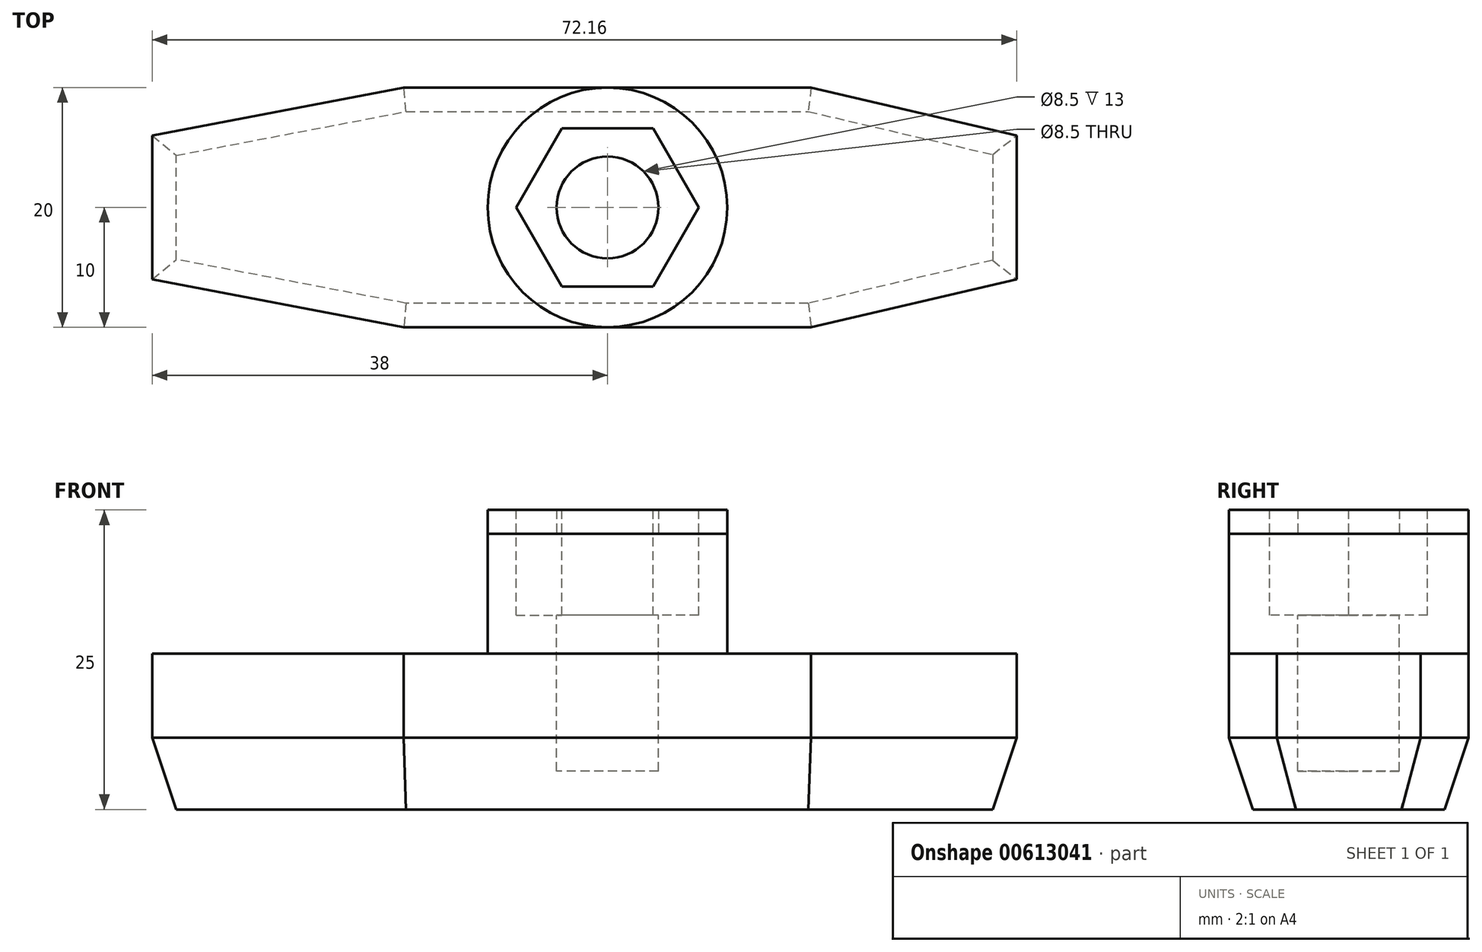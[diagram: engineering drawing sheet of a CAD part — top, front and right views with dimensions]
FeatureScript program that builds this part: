
annotation { "Feature Type Name" : "Feature", "Feature Type Description" : "" }
export const myFeature = defineFeature(function(context is Context, id is Id, definition is map)
    precondition{}
    {
        {
            var Q0;
            Q0=qCreatedBy(makeId("Top.planeOp"),FACE);
            var sketch = newSketch(context, id + "F0", { "sketchPlane" : qUnion([Q0])});
            skLineSegment(sketch, "E0.bottom", {"start": v(17, -10) * mm, "end": v(-17, -10) * mm});
            skLineSegment(sketch, "E0.top", {"start": v(17, 10) * mm, "end": v(-17, 10) * mm});
            skPoint(sketch, "E0.middle", {"position": v(0, 0) * mm});
            skLineSegment(sketch, "E1", {"start": v(-17, 10) * mm, "end": v(-38, 6) * mm});
            skLineSegment(sketch, "E2", {"start": v(-38, 6) * mm, "end": v(-38, -6) * mm});
            skLineSegment(sketch, "E3", {"start": v(-38, -6) * mm, "end": v(-17, -10) * mm});
            skLineSegment(sketch, "E4", {"start": v(17, 10) * mm, "end": v(34.16, 6) * mm});
            skLineSegment(sketch, "E5", {"start": v(34.16, 6) * mm, "end": v(34.16, -6) * mm});
            skLineSegment(sketch, "E6", {"start": v(34.16, -6) * mm, "end": v(17, -10) * mm});
            skSolve(sketch);
        }
        {
            var Q0;
            Q0=makeQuery(id+"F0.imprint","IMPRINT",FACE,{"disambiguationData":[TD([[makeQuery(id+"F0.imprint","IMPRINT",EDGE,{"derivedFrom":sQuery(id+"F0.wireOp",EDGE,"E0.bottom")}),-1.0]])]});
            extrude(context, id + "F1", {"entities" : qUnion([Q0]), "depth" : 13 * mm, "offsetDistance" : 25 * mm});
        }
        {
            var Q0;
            Q0=makeQuery(id+"F1.opExtrude","CAP_FACE",FACE,{"disambiguationData":[OSD([sQuery(id+"F0.wireOp",EDGE,"E0.bottom"),sQuery(id+"F0.wireOp",EDGE,"E0.top"),sQuery(id+"F0.wireOp",EDGE,"E1"),sQuery(id+"F0.wireOp",EDGE,"E2"),sQuery(id+"F0.wireOp",EDGE,"E3"),sQuery(id+"F0.wireOp",EDGE,"E4"),sQuery(id+"F0.wireOp",EDGE,"E5"),sQuery(id+"F0.wireOp",EDGE,"E6")])],"isStart":false});
            var sketch = newSketch(context, id + "F2", { "sketchPlane" : qUnion([Q0])});
            skCircle(sketch, "E7", {"center": v(0, 0) * mm, "radius": 10 * mm});
            skSolve(sketch);
        }
        {
            var Q0;
            {var subQ0=sQuery(id+"F2.wireOp",EDGE,"E7");var subQ1=makeQuery(id+"F2.imprint","INTERSECT",VERTEX,{"derivedFrom":[makeQuery(id+"F1.opExtrude","CAP_EDGE",EDGE,{"disambiguationData":[OSD([sQuery(id+"F0.wireOp",EDGE,"E0.bottom")])],"isStart":false}),subQ0]});Q0=makeQuery(id+"F2.imprint","IMPRINT",FACE,{"disambiguationData":[TD([[makeQuery(id+"F2.imprint","IMPRINT",EDGE,{"disambiguationData":[TD([[subQ1,1.0]])],"derivedFrom":subQ0}),1.0]])]});}
            extrude(context, id + "F3", {"entities" : qUnion([Q0]), "operationType" : NewBodyOperationType.ADD, "depth" : 12 * mm, "offsetDistance" : 25 * mm});
        }
        {
            var Q0;
            Q0=makeQuery(id+"F3.opExtrude","CAP_FACE",FACE,{"disambiguationData":[OSD([sQuery(id+"F2.wireOp",EDGE,"E7")])],"isStart":false});
            var sketch = newSketch(context, id + "F4", { "sketchPlane" : qUnion([Q0])});
            skCircle(sketch, "E8.cCircle", {"center": v(0, 0) * mm, "radius": 6.6 * mm, "construction": true});
            skLineSegment(sketch, "E8.0", {"start": v(3.81, -6.6) * mm, "end": v(-3.81, -6.6) * mm});
            skLineSegment(sketch, "E8.1", {"start": v(-3.81, -6.6) * mm, "end": v(-7.62, 0) * mm});
            skLineSegment(sketch, "E8.2", {"start": v(-7.62, 0) * mm, "end": v(-3.81, 6.6) * mm});
            skLineSegment(sketch, "E8.3", {"start": v(-3.81, 6.6) * mm, "end": v(3.81, 6.6) * mm});
            skLineSegment(sketch, "E8.4", {"start": v(3.81, 6.6) * mm, "end": v(7.62, 0) * mm});
            skLineSegment(sketch, "E8.5", {"start": v(7.62, 0) * mm, "end": v(3.81, -6.6) * mm});
            skPoint(sketch, "E8.0.midPoint", {"position": v(0, -6.6) * mm});
            skSolve(sketch);
        }
        {
            var Q0;
            Q0=makeQuery(id+"F4.imprint","IMPRINT",FACE,{"disambiguationData":[TD([[makeQuery(id+"F4.imprint","IMPRINT",EDGE,{"derivedFrom":sQuery(id+"F4.wireOp",EDGE,"E8.0")}),-1.0]])]});
            extrude(context, id + "F5", {"entities" : qUnion([Q0]), "operationType" : NewBodyOperationType.REMOVE, "oppositeDirection" : true, "depth" : 8.8 * mm, "offsetDistance" : 25 * mm});
        }
        {
            var Q0;
            Q0=makeQuery(id+"F5.boolean.opBoolean","COPY",FACE,{"derivedFrom":makeQuery(id+"F5.opExtrude","CAP_FACE",FACE,{"disambiguationData":[OSD([sQuery(id+"F4.wireOp",EDGE,"E8.0"),sQuery(id+"F4.wireOp",EDGE,"E8.1"),sQuery(id+"F4.wireOp",EDGE,"E8.2"),sQuery(id+"F4.wireOp",EDGE,"E8.3"),sQuery(id+"F4.wireOp",EDGE,"E8.4"),sQuery(id+"F4.wireOp",EDGE,"E8.5")])],"isStart":false})});
            var sketch = newSketch(context, id + "F6", { "sketchPlane" : qUnion([Q0])});
            skCircle(sketch, "E9", {"center": v(0, 0) * mm, "radius": 4.25 * mm});
            skSolve(sketch);
        }
        {
            var Q0;
            Q0=makeQuery(id+"F6.imprint","IMPRINT",FACE,{"disambiguationData":[TD([[makeQuery(id+"F6.imprint","IMPRINT",EDGE,{"derivedFrom":sQuery(id+"F6.wireOp",EDGE,"E9")}),1.0]])]});
            extrude(context, id + "F7", {"entities" : qUnion([Q0]), "operationType" : NewBodyOperationType.REMOVE, "oppositeDirection" : true, "depth" : 13 * mm, "offsetDistance" : 25 * mm});
        }
        {
            var Q0;
            Q0=qCreatedBy(makeId("Top.planeOp"),FACE);
            cPlane(context, id + "F8", {"entities" : qUnion([Q0]), "cplaneType" : CPlaneType.OFFSET, "offset" : 23 * mm, "width" : 150 * mm, "height" : 150 * mm});
        }
        {
            var Q0;
            Q0=qCreatedBy(id+"F8.planeOp",FACE);
            var sketch = newSketch(context, id + "F9", { "sketchPlane" : qUnion([Q0])});
            skCircle(sketch, "E10", {"center": v(0, 0) * mm, "radius": 10 * mm});
            skCircle(sketch, "E11", {"center": v(0, 0) * mm, "radius": 4.25 * mm});
            skSolve(sketch);
        }
        {
            var Q0;
            Q0=makeQuery(id+"F9.imprint","IMPRINT",FACE,{"disambiguationData":[TD([[makeQuery(id+"F9.imprint","IMPRINT",EDGE,{"derivedFrom":sQuery(id+"F9.wireOp",EDGE,"E10")}),1.0]])]});
            extrude(context, id + "F10", {"entities" : qUnion([Q0]), "depth" : 2 * mm, "offsetDistance" : 25 * mm});
        }
        {
            var Q0;
            Q0=makeQuery(id+"F1.opExtrude","CAP_EDGE",EDGE,{"disambiguationData":[OSD([sQuery(id+"F0.wireOp",EDGE,"E0.bottom")])],"isStart":true});
            var Q1;
            Q1=makeQuery(id+"F1.opExtrude","CAP_EDGE",EDGE,{"disambiguationData":[OSD([sQuery(id+"F0.wireOp",EDGE,"E3")])],"isStart":true});
            var Q2;
            Q2=makeQuery(id+"F1.opExtrude","CAP_EDGE",EDGE,{"disambiguationData":[OSD([sQuery(id+"F0.wireOp",EDGE,"E2")])],"isStart":true});
            var Q3;
            Q3=makeQuery(id+"F1.opExtrude","CAP_EDGE",EDGE,{"disambiguationData":[OSD([sQuery(id+"F0.wireOp",EDGE,"E6")])],"isStart":true});
            var Q4;
            Q4=makeQuery(id+"F1.opExtrude","CAP_EDGE",EDGE,{"disambiguationData":[OSD([sQuery(id+"F0.wireOp",EDGE,"E5")])],"isStart":true});
            var Q5;
            Q5=makeQuery(id+"F1.opExtrude","CAP_EDGE",EDGE,{"disambiguationData":[OSD([sQuery(id+"F0.wireOp",EDGE,"E4")])],"isStart":true});
            var Q6;
            Q6=makeQuery(id+"F1.opExtrude","CAP_EDGE",EDGE,{"disambiguationData":[OSD([sQuery(id+"F0.wireOp",EDGE,"E0.top")])],"isStart":true});
            var Q7;
            Q7=makeQuery(id+"F1.opExtrude","CAP_EDGE",EDGE,{"disambiguationData":[OSD([sQuery(id+"F0.wireOp",EDGE,"E1")])],"isStart":true});
            chamfer(context, id + "F11", {"entities" : qUnion([Q0, Q1, Q2, Q3, Q4, Q5, Q6, Q7]), "chamferType" : ChamferType.TWO_OFFSETS, "width1" : 2 * mm, "oppositeDirection" : false, "width2" : 6 * mm, "tangentPropagation" : true});
        }
    });
